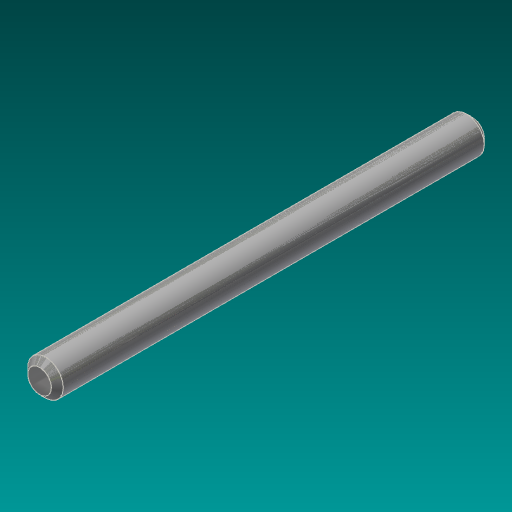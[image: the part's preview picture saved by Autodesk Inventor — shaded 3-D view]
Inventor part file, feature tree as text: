
AUTODESK INVENTOR PART (.ipt)
format: ipt  version: 2017.3 (Build 213256000, 256)  size: 111,616 bytes
history: native  units: in
note: dims shown in document units (in); Inventor stores cm internally (conversion verified against a paired STEP export)
features: extrude x1, chamfer x1, sketch x1
ambient origin geometry x8: Origin, YZ Plane, XZ Plane, XY Plane, X Axis, Y Axis, Z Axis, Center Point
bodies: Solid1 (feature_tree)
feature tree (3):
  extrude  "Extrusion1"  Depth=4.5625in TaperAngle=0.0deg
  chamfer  "Chamfer1"  Distance=0.0625in Angle=45.0deg
  sketch  "Sketch1"  dims[d0=0.375in d1=4.5625in d2=0.0in d3=0.0625in d4=0.125in d5=45.0deg]
